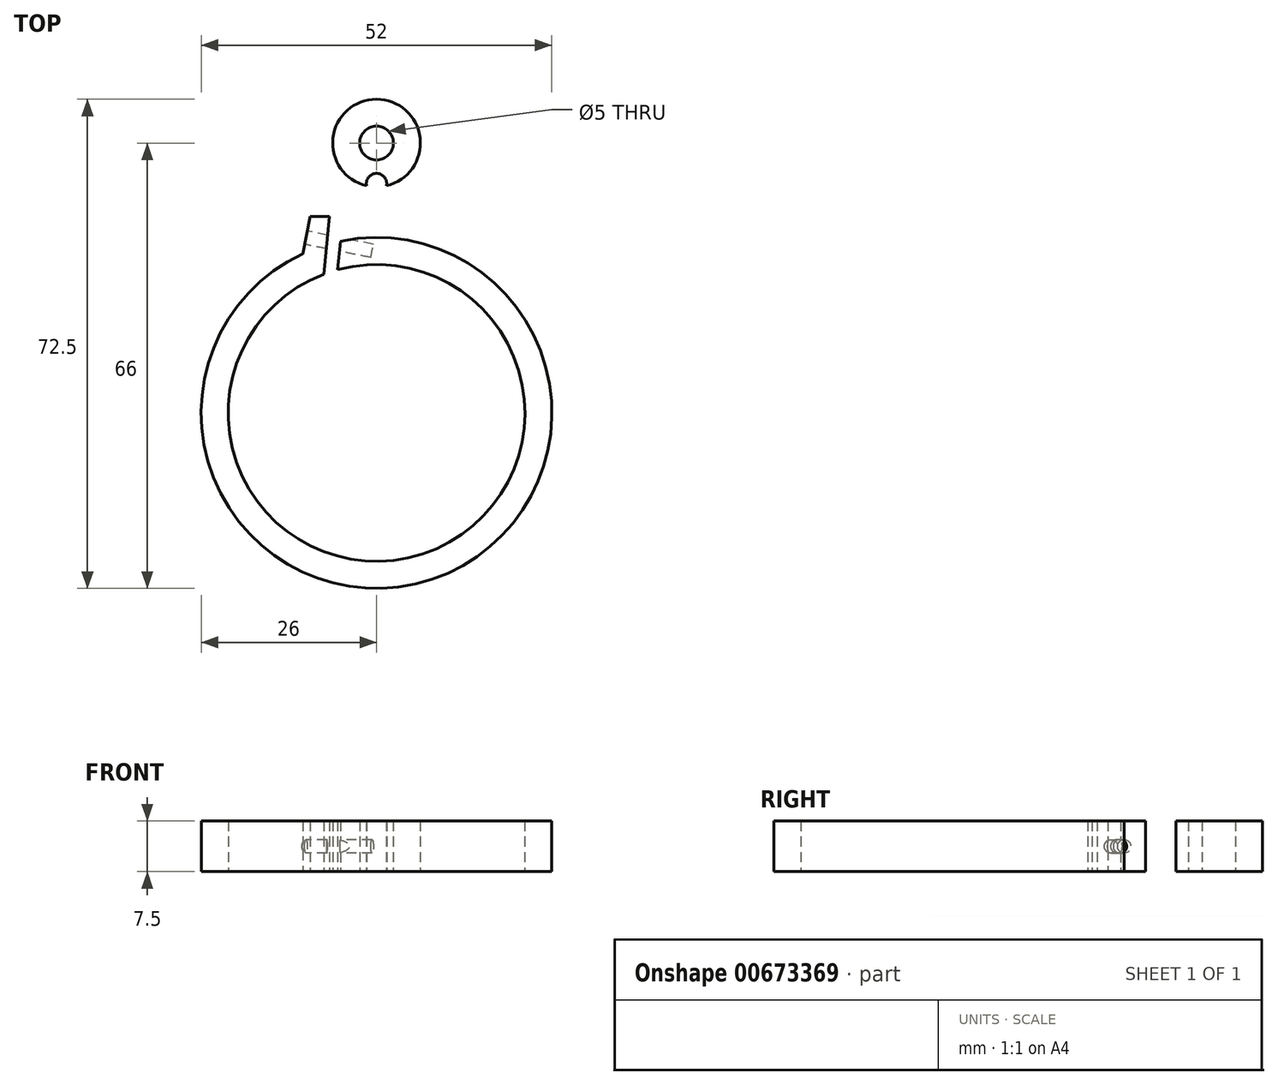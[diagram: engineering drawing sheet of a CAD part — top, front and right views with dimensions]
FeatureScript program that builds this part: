
annotation { "Feature Type Name" : "Feature", "Feature Type Description" : "" }
export const myFeature = defineFeature(function(context is Context, id is Id, definition is map)
    precondition{}
    {
        {
            var Q0;
            Q0=qCreatedBy(makeId("Top.planeOp"),FACE);
            var sketch = newSketch(context, id + "F0", { "sketchPlane" : qUnion([Q0])});
            skCircle(sketch, "E0", {"center": v(0, 0) * mm, "radius": 26 * mm});
            skCircle(sketch, "E1", {"center": v(0, 0) * mm, "radius": 22 * mm});
            skCircle(sketch, "E2", {"center": v(0, 40) * mm, "radius": 6.5 * mm});
            skArc(sketch, "E3", {"start": v(-9.81, 24.08) * mm, "mid": v(-4.8, 29.4) * mm, "end": v(-5.59, 36.68) * mm});
            skArc(sketch, "E4.MirrorCS", {"start": v(9.81, 24.08) * mm, "mid": v(4.8, 29.4) * mm, "end": v(5.59, 36.68) * mm});
            skCircle(sketch, "E5", {"center": v(0, 40) * mm, "radius": 2.5 * mm});
            skCircle(sketch, "E6", {"center": v(0, 34) * mm, "radius": 1.5 * mm});
            skLineSegment(sketch, "E7", {"start": v(-9.84, 29.13) * mm, "end": v(-15.65, 0) * mm});
            skLineSegment(sketch, "E8", {"start": v(-5.9, 29.83) * mm, "end": v(-7.02, 18.51) * mm});
            skArc(sketch, "E9.0.startCap", {"start": v(-6.9, 29.93) * mm, "mid": v(-5.81, 30.83) * mm, "end": v(-4.91, 29.73) * mm});
            skArc(sketch, "E9.0.endCap", {"start": v(-6.02, 18.41) * mm, "mid": v(-7.12, 17.51) * mm, "end": v(-8.01, 18.6) * mm});
            skLineSegment(sketch, "E9.0.left", {"start": v(-4.91, 29.73) * mm, "end": v(-6.02, 18.41) * mm});
            skLineSegment(sketch, "E9.0.right", {"start": v(-6.9, 29.93) * mm, "end": v(-8.01, 18.6) * mm});
            skPoint(sketch, "E10", {"position": v(-4.8, 29.4) * mm});
            skLineSegment(sketch, "E11", {"start": v(-9.84, 29.13) * mm, "end": v(-2.6, 29.13) * mm});
            skSolve(sketch);
        }
        {
            var Q0;
            Q0=makeQuery(id+"F0.imprint","IMPRINT",FACE,{"disambiguationData":[TD([[makeQuery(id+"F0.imprint","IMPRINT",EDGE,{"derivedFrom":sQuery(id+"F0.wireOp",EDGE,"E5")}),-1.0]])]});
            var Q1;
            {var subQ5=sQuery(id+"F0.wireOp",EDGE,"E4.MirrorCS");Q1=makeQuery(id+"F0.imprint","IMPRINT",FACE,{"disambiguationData":[TD([[makeQuery(id+"F0.imprint","IMPRINT",EDGE,{"derivedFrom":subQ5}),1.0]])]});}
            var Q2;
            {var subQ5=sQuery(id+"F0.wireOp",EDGE,"E0");var subQ8=makeQuery(id+"F0.imprint","INTERSECT",VERTEX,{"derivedFrom":[subQ5,sQuery(id+"F0.wireOp",EDGE,"E4.MirrorCS")]});Q2=makeQuery(id+"F0.imprint","IMPRINT",FACE,{"disambiguationData":[TD([[makeQuery(id+"F0.imprint","IMPRINT",EDGE,{"disambiguationData":[TD([[subQ8,-1.0]])],"derivedFrom":subQ5}),1.0]])]});}
            var Q3;
            {var subQ0=sQuery(id+"F0.wireOp",EDGE,"E9.0.right");var subQ1=sQuery(id+"F0.wireOp",EDGE,"E0");var subQ2=makeQuery(id+"F0.imprint","INTERSECT",VERTEX,{"derivedFrom":[subQ1,subQ0]});Q3=makeQuery(id+"F0.imprint","IMPRINT",FACE,{"disambiguationData":[TD([[makeQuery(id+"F0.imprint","IMPRINT",EDGE,{"disambiguationData":[TD([[subQ2,-1.0]])],"derivedFrom":subQ1}),1.0]])]});}
            var Q4;
            {var subQ0=sQuery(id+"F0.wireOp",EDGE,"E9.0.right");var subQ1=sQuery(id+"F0.wireOp",EDGE,"E0");var subQ2=makeQuery(id+"F0.imprint","INTERSECT",VERTEX,{"derivedFrom":[subQ1,subQ0]});Q4=makeQuery(id+"F0.imprint","IMPRINT",FACE,{"disambiguationData":[TD([[makeQuery(id+"F0.imprint","IMPRINT",EDGE,{"disambiguationData":[TD([[subQ2,-1.0]])],"derivedFrom":subQ1}),-1.0]])]});}
            var Q5;
            {var subQ3=sQuery(id+"F0.wireOp",EDGE,"E3");var subQ5=sQuery(id+"F0.wireOp",EDGE,"E0");var subQ6=makeQuery(id+"F0.imprint","INTERSECT",VERTEX,{"derivedFrom":[subQ5,subQ3]});Q5=makeQuery(id+"F0.imprint","IMPRINT",FACE,{"disambiguationData":[TD([[makeQuery(id+"F0.imprint","IMPRINT",EDGE,{"disambiguationData":[TD([[subQ6,-1.0]])],"derivedFrom":subQ5}),-1.0]])]});}
            extrude(context, id + "F1", {"entities" : qUnion([Q0, Q1, Q2, Q3, Q4, Q5]), "depth" : 7.5 * mm, "offsetDistance" : 25 * mm});
        }
        {
            var Q0;
            Q0=makeQuery(id+"F1.opExtrude","SWEPT_FACE",FACE,{"disambiguationData":[OSD([sQuery(id+"F0.wireOp",EDGE,"E7")])]});
            var sketch = newSketch(context, id + "F2", { "sketchPlane" : qUnion([Q0])});
            skCircle(sketch, "E12", {"center": v(-23.42, 3.75) * mm, "radius": 1 * mm});
            skCircle(sketch, "E13", {"center": v(-23.42, 3.75) * mm, "radius": 2.5 * mm});
            skSolve(sketch);
        }
        {
            var Q0;
            Q0=makeQuery(id+"F2.imprint","IMPRINT",FACE,{"disambiguationData":[TD([[makeQuery(id+"F2.imprint","IMPRINT",EDGE,{"derivedFrom":sQuery(id+"F2.wireOp",EDGE,"E12")}),1.0]])]});
            extrude(context, id + "F3", {"entities" : qUnion([Q0]), "operationType" : NewBodyOperationType.REMOVE, "oppositeDirection" : true, "depth" : 10 * mm, "offsetDistance" : 25 * mm});
        }
        {
            var Q0;
            {var subQ0=sQuery(id+"F2.wireOp",EDGE,"E13");var subQ1=makeQuery(id+"F1.opExtrude","SWEPT_EDGE",EDGE,{"disambiguationData":[OSD([sQuery(id+"F0.wireOp",EDGE,"E0"),sQuery(id+"F0.wireOp",EDGE,"E7")])]});var subQ2=makeQuery(id+"F2.imprint","INTERSECT",VERTEX,{"disambiguationData":[OD(0.0)],"derivedFrom":[subQ1,subQ0]});Q0=makeQuery(id+"F2.imprint","IMPRINT",FACE,{"disambiguationData":[TD([[makeQuery(id+"F2.imprint","IMPRINT",EDGE,{"disambiguationData":[TD([[subQ2,1.0]])],"derivedFrom":subQ0}),1.0]])]});}
            var Q1;
            {var subQ0=sQuery(id+"F2.wireOp",EDGE,"E13");var subQ1=makeQuery(id+"F1.opExtrude","SWEPT_EDGE",EDGE,{"disambiguationData":[OSD([sQuery(id+"F0.wireOp",EDGE,"E0"),sQuery(id+"F0.wireOp",EDGE,"E7")])]});var subQ2=makeQuery(id+"F2.imprint","INTERSECT",VERTEX,{"disambiguationData":[OD(0.0)],"derivedFrom":[subQ1,subQ0]});Q1=makeQuery(id+"F2.imprint","IMPRINT",FACE,{"disambiguationData":[TD([[makeQuery(id+"F2.imprint","IMPRINT",EDGE,{"disambiguationData":[TD([[subQ2,-1.0]])],"derivedFrom":subQ0}),1.0]])]});}
            extrude(context, id + "F4", {"entities" : qUnion([Q0, Q1]), "operationType" : NewBodyOperationType.REMOVE, "depth" : 25 * mm, "offsetDistance" : 25 * mm});
        }
    });
